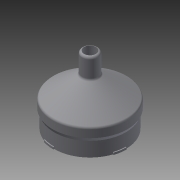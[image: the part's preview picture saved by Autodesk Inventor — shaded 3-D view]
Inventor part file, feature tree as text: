
AUTODESK INVENTOR PART (.ipt)
format: ipt  version: 2014 SP1 (Build 180222100, 222)  size: 199,168 bytes
history: native  units: in
note: dims shown in document units (in); Inventor stores cm internally (conversion verified against a paired STEP export)
features: plane x1, revolve x1, extrude x1, sketch x1
ambient origin geometry x8: Origin, YZ Plane, XZ Plane, XY Plane, X Axis, Y Axis, Z Axis, Center Point
bodies: Body1 (feature_tree)
feature tree (4):
  plane  "Work Plane1"
  revolve  "Revolution5"  [1 undecoded]
  extrude  "Extrusion7"  Depth=0.1in
  sketch  "Sketch8"  dims[d9=1.0in d10=0.3in d11=0.1in d16=1.0in d18=0.125in d19=0.125in d24=1.875in d26=0.35in d47=1.0in d53=1.792in d55=0.0673in d56=0.9in d58=90.0deg d68=0.067in d72=15.0deg d75=105.0deg d78=165.0deg d81=75.0deg d82=0.1in d83=0.0in d84=0.725in d85=3.25in d86=0.15in]
note: 1 required parameter value undecoded (feature->parameter linkage not recoverable at this tier; creation-order binding heuristic only, values carry confidence <= 0.55)
